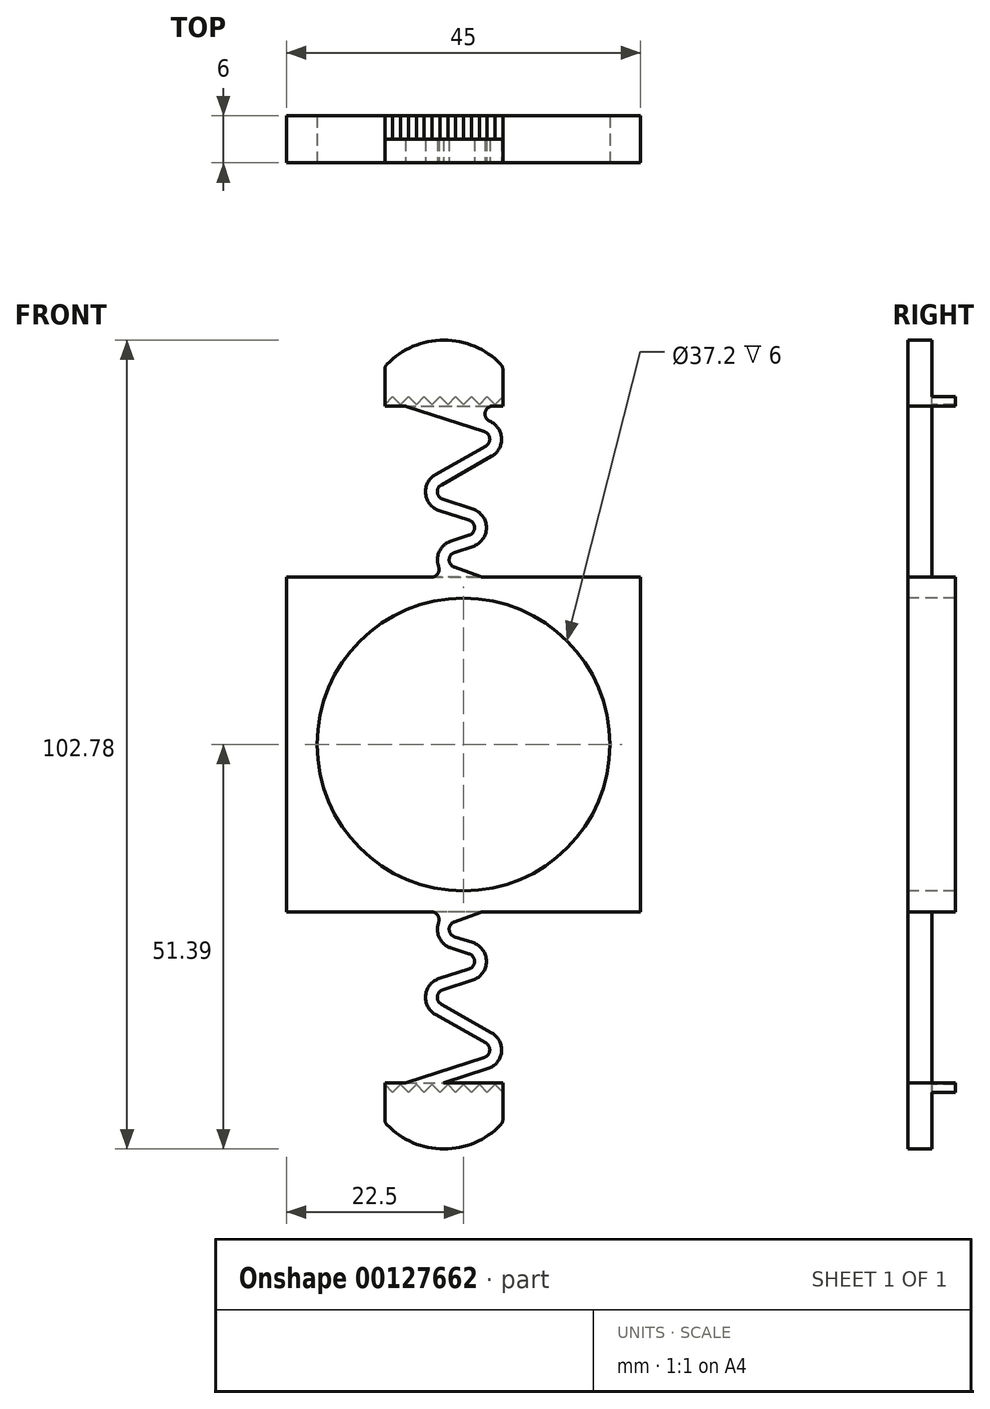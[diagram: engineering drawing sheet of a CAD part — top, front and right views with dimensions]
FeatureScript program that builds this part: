
annotation { "Feature Type Name" : "Feature", "Feature Type Description" : "" }
export const myFeature = defineFeature(function(context is Context, id is Id, definition is map)
    precondition{}
    {
        {
            var Q0;
            Q0=qCreatedBy(makeId("Right.planeOp"),FACE);
            var sketch = newSketch(context, id + "F0", { "sketchPlane" : qUnion([Q0])});
            skLineSegment(sketch, "E0", {"start": v(0, 25) * mm, "end": v(0, -25) * mm});
            skLineSegment(sketch, "E1", {"start": v(0, -25) * mm, "end": v(-3, -25) * mm});
            skLineSegment(sketch, "E2", {"start": v(-3, -25) * mm, "end": v(-3, -21.25) * mm});
            skLineSegment(sketch, "E3", {"start": v(-3, -21.25) * mm, "end": v(-9, -21.25) * mm});
            skLineSegment(sketch, "E4", {"start": v(-9, -21.25) * mm, "end": v(-9, 21.25) * mm});
            skLineSegment(sketch, "E5", {"start": v(-9, 21.25) * mm, "end": v(-3, 21.25) * mm});
            skLineSegment(sketch, "E6", {"start": v(-3, 21.25) * mm, "end": v(-3, 25) * mm});
            skLineSegment(sketch, "E7", {"start": v(-3, 25) * mm, "end": v(0, 25) * mm});
            skSolve(sketch);
        }
        {
            var Q0;
            Q0 = qSketchRegion(id + "F0", true);
            extrude(context, id + "F1", {"entities" : qUnion([Q0]), "endBound" : BoundingType.SYMMETRIC, "depth" : 45 * mm});
        }
        {
            var Q0;
            Q0=makeQuery(id+"F1.opExtrude","SWEPT_FACE",FACE,{"disambiguationData":[OSD([sQuery(id+"F0.wireOp",EDGE,"E4")])]});
            var sketch = newSketch(context, id + "F2", { "sketchPlane" : qUnion([Q0])});
            skCircle(sketch, "E8", {"center": v(0, 0) * mm, "radius": 18.6 * mm});
            skSolve(sketch);
        }
        {
            var Q0;
            Q0 = qSketchRegion(id + "F2", true);
            extrude(context, id + "F3", {"entities" : qUnion([Q0]), "operationType" : NewBodyOperationType.REMOVE, "oppositeDirection" : true, "depth" : 6 * mm});
        }
        {
            var Q0;
            Q0=makeQuery(id+"F3.boolean.opBoolean","COPY",FACE,{"derivedFrom":makeQuery(id+"F3.opExtrude","CAP_FACE",FACE,{"disambiguationData":[OSD([sQuery(id+"F2.wireOp",EDGE,"E8")])],"isStart":false})});
            var sketch = newSketch(context, id + "F4", { "sketchPlane" : qUnion([Q0])});
            skCircle(sketch, "E9", {"center": v(0, 0) * mm, "radius": 17.5 * mm});
            skSolve(sketch);
        }
        {
            var Q0;
            Q0 = qSketchRegion(id + "F4", true);
            extrude(context, id + "F5", {"entities" : qUnion([Q0]), "operationType" : NewBodyOperationType.REMOVE, "endBound" : BoundingType.UP_TO_NEXT, "oppositeDirection" : true, "depth" : 25 * mm});
        }
        {
            var Q0;
            Q0=makeQuery(id+"F1.opExtrude","SWEPT_FACE",FACE,{"disambiguationData":[OSD([sQuery(id+"F0.wireOp",EDGE,"E4")])]});
            var sketch = newSketch(context, id + "F6", { "sketchPlane" : qUnion([Q0])});
            skLineSegment(sketch, "E10", {"start": v(0, 43.5) * mm, "end": v(0, -43.5) * mm, "construction": true});
            skLineSegment(sketch, "E11", {"start": v(-1.5, 21.05) * mm, "end": v(-1.68, 21.11) * mm});
            skLineSegment(sketch, "E12", {"start": v(-1.6, 25.84) * mm, "end": v(0.72, 26.6) * mm});
            skLineSegment(sketch, "E13", {"start": v(0.72, 28.5) * mm, "end": v(-3.1, 29.74) * mm});
            skLineSegment(sketch, "E14", {"start": v(-3.57, 34.29) * mm, "end": v(2.83, 37.92) * mm});
            skLineSegment(sketch, "E15", {"start": v(2.64, 39.74) * mm, "end": v(-8.93, 43.5) * mm});
            skLineSegment(sketch, "E16", {"start": v(-8.5, 31.5) * mm, "end": v(-8.5, 23.6) * mm, "construction": true});
            skLineSegment(sketch, "E17", {"start": v(-1.13, 24.41) * mm, "end": v(1.18, 25.17) * mm});
            skLineSegment(sketch, "E18", {"start": v(1.18, 29.92) * mm, "end": v(-2.64, 31.16) * mm});
            skLineSegment(sketch, "E19", {"start": v(-2.83, 32.99) * mm, "end": v(3.57, 36.61) * mm});
            skLineSegment(sketch, "E20", {"start": v(3.1, 41.17) * mm, "end": v(-4.08, 43.5) * mm});
            skLineSegment(sketch, "E21", {"start": v(8.5, 39.41) * mm, "end": v(8.5, 27.54) * mm, "construction": true});
            skLineSegment(sketch, "E22", {"start": v(-8.93, 43.5) * mm, "end": v(-4.08, 43.5) * mm});
            skPoint(sketch, "E23.visualSharp", {"position": v(-4.8, 31.87) * mm});
            skArc(sketch, "E23.filletArc", {"start": v(-2.83, 32.99) * mm, "mid": v(-3.33, 32.01) * mm, "end": v(-2.64, 31.16) * mm});
            skPoint(sketch, "E24.visualSharp", {"position": v(-4.56, 23.3) * mm});
            skArc(sketch, "E24.filletArc", {"start": v(-1.13, 24.41) * mm, "mid": v(-1.82, 23.48) * mm, "end": v(-1.16, 22.52) * mm});
            skPoint(sketch, "E25.visualSharp", {"position": v(3.65, 27.54) * mm});
            skArc(sketch, "E25.filletArc", {"start": v(0.72, 26.6) * mm, "mid": v(1.4, 27.54) * mm, "end": v(0.72, 28.5) * mm});
            skPoint(sketch, "E26.visualSharp", {"position": v(4.8, 39.04) * mm});
            skArc(sketch, "E26.filletArc", {"start": v(2.83, 37.92) * mm, "mid": v(3.33, 38.89) * mm, "end": v(2.64, 39.74) * mm});
            skPoint(sketch, "E27.visualSharp", {"position": v(8.5, 39.41) * mm});
            skArc(sketch, "E27.filletArc", {"start": v(3.57, 36.61) * mm, "mid": v(4.82, 39.04) * mm, "end": v(3.1, 41.17) * mm});
            skPoint(sketch, "E28.visualSharp", {"position": v(-8.5, 31.5) * mm});
            skArc(sketch, "E28.filletArc", {"start": v(-3.57, 34.29) * mm, "mid": v(-4.82, 31.86) * mm, "end": v(-3.1, 29.74) * mm});
            skPoint(sketch, "E29.visualSharp", {"position": v(8.5, 27.54) * mm});
            skArc(sketch, "E29.filletArc", {"start": v(1.18, 25.17) * mm, "mid": v(2.9, 27.54) * mm, "end": v(1.18, 29.92) * mm});
            skPoint(sketch, "E30.visualSharp", {"position": v(-8.5, 23.6) * mm});
            skArc(sketch, "E30.filletArc", {"start": v(-1.6, 25.84) * mm, "mid": v(-3.32, 23.5) * mm, "end": v(-1.68, 21.11) * mm});
            skLineSegment(sketch, "E31", {"start": v(0, 0) * mm, "end": v(22.5, 0) * mm, "construction": true});
            skArc(sketch, "E32.MirrorCS", {"start": v(-2.83, -32.99) * mm, "mid": v(-3.33, -32.01) * mm, "end": v(-2.64, -31.16) * mm});
            skArc(sketch, "E33.MirrorCS", {"start": v(2.83, -37.92) * mm, "mid": v(3.33, -38.89) * mm, "end": v(2.64, -39.74) * mm});
            skArc(sketch, "E34.MirrorCS", {"start": v(-1.13, -24.41) * mm, "mid": v(-1.82, -23.48) * mm, "end": v(-1.16, -22.52) * mm});
            skLineSegment(sketch, "E35.MirrorCS", {"start": v(3.1, -41.17) * mm, "end": v(-4.08, -43.5) * mm});
            skLineSegment(sketch, "E36.MirrorCS", {"start": v(-1.5, -21.05) * mm, "end": v(-1.68, -21.11) * mm});
            skArc(sketch, "E37.MirrorCS", {"start": v(0.72, -26.6) * mm, "mid": v(1.4, -27.54) * mm, "end": v(0.72, -28.5) * mm});
            skArc(sketch, "E38.MirrorCS", {"start": v(1.18, -25.17) * mm, "mid": v(2.9, -27.54) * mm, "end": v(1.18, -29.92) * mm});
            skArc(sketch, "E39.MirrorCS", {"start": v(3.57, -36.61) * mm, "mid": v(4.82, -39.04) * mm, "end": v(3.1, -41.17) * mm});
            skArc(sketch, "E40.MirrorCS", {"start": v(-3.57, -34.29) * mm, "mid": v(-4.82, -31.86) * mm, "end": v(-3.1, -29.74) * mm});
            skLineSegment(sketch, "E41.MirrorCS", {"start": v(-1.13, -24.41) * mm, "end": v(1.18, -25.17) * mm});
            skLineSegment(sketch, "E42.MirrorCS", {"start": v(-2.83, -32.99) * mm, "end": v(3.57, -36.61) * mm});
            skLineSegment(sketch, "E43.MirrorCS", {"start": v(2.64, -39.74) * mm, "end": v(-8.93, -43.5) * mm});
            skLineSegment(sketch, "E44.MirrorCS", {"start": v(-3.57, -34.29) * mm, "end": v(2.83, -37.92) * mm});
            skLineSegment(sketch, "E45.MirrorCS", {"start": v(0.72, -28.5) * mm, "end": v(-3.1, -29.74) * mm});
            skLineSegment(sketch, "E46.MirrorCS", {"start": v(-1.6, -25.84) * mm, "end": v(0.72, -26.6) * mm});
            skPoint(sketch, "E47.MirrorP", {"position": v(-4.56, -23.3) * mm});
            skPoint(sketch, "E48.MirrorP", {"position": v(4.8, -39.04) * mm});
            skLineSegment(sketch, "E49.MirrorCS", {"start": v(-8.93, -43.5) * mm, "end": v(-4.08, -43.5) * mm});
            skLineSegment(sketch, "E50.MirrorCS", {"start": v(1.18, -29.92) * mm, "end": v(-2.64, -31.16) * mm});
            skPoint(sketch, "E51.MirrorP", {"position": v(-8.5, -31.5) * mm});
            skPoint(sketch, "E52.MirrorP", {"position": v(8.5, -27.54) * mm});
            skPoint(sketch, "E53.MirrorP", {"position": v(3.65, -27.54) * mm});
            skPoint(sketch, "E54.MirrorP", {"position": v(8.5, -39.41) * mm});
            skPoint(sketch, "E55.MirrorP", {"position": v(-8.5, -23.6) * mm});
            skArc(sketch, "E56.MirrorCS", {"start": v(-1.6, -25.84) * mm, "mid": v(-3.32, -23.5) * mm, "end": v(-1.68, -21.11) * mm});
            skPoint(sketch, "E57.MirrorP", {"position": v(-4.8, -31.87) * mm});
            skPoint(sketch, "E58.orphan", {"position": v(1.5, 21.25) * mm});
            skLineSegment(sketch, "E59", {"start": v(-1.5, 21.05) * mm, "end": v(2.89, 21.05) * mm});
            skLineSegment(sketch, "E60", {"start": v(2.89, 21.05) * mm, "end": v(-1.16, 22.52) * mm});
            skLineSegment(sketch, "E61", {"start": v(-1.5, -21.05) * mm, "end": v(2.89, -21.05) * mm});
            skLineSegment(sketch, "E62", {"start": v(2.89, -21.05) * mm, "end": v(-1.16, -22.52) * mm});
            skSolve(sketch);
        }
        {
            var Q0;
            Q0 = qSketchRegion(id + "F6", true);
            extrude(context, id + "F7", {"entities" : qUnion([Q0]), "operationType" : NewBodyOperationType.ADD, "oppositeDirection" : true, "depth" : 3 * mm});
        }
        {
            var Q0;
            Q0=makeQuery(id+"F7.boolean.opBoolean","MERGE",FACE,{"derivedFrom":[makeQuery(id+"F1.opExtrude","SWEPT_FACE",FACE,{"disambiguationData":[OSD([sQuery(id+"F0.wireOp",EDGE,"E4")])]}),makeQuery(id+"F7.opExtrude","CAP_FACE",FACE,{"disambiguationData":[OSD([sQuery(id+"F6.wireOp",EDGE,"E11"),sQuery(id+"F6.wireOp",EDGE,"E12"),sQuery(id+"F6.wireOp",EDGE,"E13"),sQuery(id+"F6.wireOp",EDGE,"E14"),sQuery(id+"F6.wireOp",EDGE,"E15"),sQuery(id+"F6.wireOp",EDGE,"E17"),sQuery(id+"F6.wireOp",EDGE,"E18"),sQuery(id+"F6.wireOp",EDGE,"E19"),sQuery(id+"F6.wireOp",EDGE,"E20"),sQuery(id+"F6.wireOp",EDGE,"E22"),sQuery(id+"F6.wireOp",EDGE,"E23.filletArc"),sQuery(id+"F6.wireOp",EDGE,"E24.filletArc"),sQuery(id+"F6.wireOp",EDGE,"E25.filletArc"),sQuery(id+"F6.wireOp",EDGE,"E26.filletArc"),sQuery(id+"F6.wireOp",EDGE,"E27.filletArc"),sQuery(id+"F6.wireOp",EDGE,"E28.filletArc"),sQuery(id+"F6.wireOp",EDGE,"E29.filletArc"),sQuery(id+"F6.wireOp",EDGE,"E30.filletArc"),sQuery(id+"F6.wireOp",EDGE,"E59"),sQuery(id+"F6.wireOp",EDGE,"E60")])],"isStart":true}),makeQuery(id+"F7.opExtrude","CAP_FACE",FACE,{"disambiguationData":[OSD([sQuery(id+"F6.wireOp",EDGE,"E32.MirrorCS"),sQuery(id+"F6.wireOp",EDGE,"E33.MirrorCS"),sQuery(id+"F6.wireOp",EDGE,"E34.MirrorCS"),sQuery(id+"F6.wireOp",EDGE,"E35.MirrorCS"),sQuery(id+"F6.wireOp",EDGE,"E36.MirrorCS"),sQuery(id+"F6.wireOp",EDGE,"E37.MirrorCS"),sQuery(id+"F6.wireOp",EDGE,"E38.MirrorCS"),sQuery(id+"F6.wireOp",EDGE,"E39.MirrorCS"),sQuery(id+"F6.wireOp",EDGE,"E40.MirrorCS"),sQuery(id+"F6.wireOp",EDGE,"E41.MirrorCS"),sQuery(id+"F6.wireOp",EDGE,"E42.MirrorCS"),sQuery(id+"F6.wireOp",EDGE,"E43.MirrorCS"),sQuery(id+"F6.wireOp",EDGE,"E44.MirrorCS"),sQuery(id+"F6.wireOp",EDGE,"E45.MirrorCS"),sQuery(id+"F6.wireOp",EDGE,"E46.MirrorCS"),sQuery(id+"F6.wireOp",EDGE,"E49.MirrorCS"),sQuery(id+"F6.wireOp",EDGE,"E50.MirrorCS"),sQuery(id+"F6.wireOp",EDGE,"E56.MirrorCS"),sQuery(id+"F6.wireOp",EDGE,"E61"),sQuery(id+"F6.wireOp",EDGE,"E62")])],"isStart":true})]});
            var sketch = newSketch(context, id + "F11", { "sketchPlane" : qUnion([Q0])});
            skLineSegment(sketch, "E63", {"start": v(-10, 43) * mm, "end": v(5, 43) * mm});
            skLineSegment(sketch, "E64", {"start": v(-10, 43) * mm, "end": v(-10, 47.61) * mm});
            skLineSegment(sketch, "E65", {"start": v(5, 47.61) * mm, "end": v(5, 43) * mm});
            skArc(sketch, "E66", {"start": v(4.72, 48.3) * mm, "mid": v(-2.5, 51.39) * mm, "end": v(-9.72, 48.3) * mm});
            skLineSegment(sketch, "E67", {"start": v(-2.5, 43.5) * mm, "end": v(-2.5, 43) * mm, "construction": true});
            skPoint(sketch, "E68.visualSharp", {"position": v(-11.33, 62.8) * mm});
            skPoint(sketch, "E69.visualSharp", {"position": v(-10, 48) * mm});
            skArc(sketch, "E69.filletArc", {"start": v(-9.72, 48.3) * mm, "mid": v(-9.93, 47.98) * mm, "end": v(-10, 47.61) * mm});
            skPoint(sketch, "E70.visualSharp", {"position": v(5, 48) * mm});
            skArc(sketch, "E70.filletArc", {"start": v(5, 47.61) * mm, "mid": v(4.93, 47.98) * mm, "end": v(4.72, 48.3) * mm});
            skLineSegment(sketch, "E71", {"start": v(0, 0) * mm, "end": v(18.6, 0) * mm, "construction": true});
            skLineSegment(sketch, "E72", {"start": v(-2.5, 47.61) * mm, "end": v(-2.5, 51.39) * mm, "construction": true});
            skLineSegment(sketch, "E73", {"start": v(-2.5, 47.61) * mm, "end": v(-10, 47.61) * mm, "construction": true});
            skPoint(sketch, "E74.MirrorCS.end.orphan", {"position": v(5, -43) * mm});
            skPoint(sketch, "E74.MirrorCS.start.orphan", {"position": v(-10, -43) * mm});
            skPoint(sketch, "E75.MirrorCS.end.orphan", {"position": v(-10, -47.61) * mm});
            skPoint(sketch, "E76.MirrorCS.start.orphan", {"position": v(5, -47.61) * mm});
            skPoint(sketch, "E77.MirrorCS.end.orphan", {"position": v(-9.72, -48.3) * mm});
            skPoint(sketch, "E77.MirrorCS.start.orphan", {"position": v(4.72, -48.3) * mm});
            skLineSegment(sketch, "E78.MirrorCS", {"start": v(-10, -43) * mm, "end": v(5, -43) * mm});
            skLineSegment(sketch, "E79.MirrorCS", {"start": v(-10, -43) * mm, "end": v(-10, -47.61) * mm});
            skArc(sketch, "E80.MirrorCS", {"start": v(4.72, -48.3) * mm, "mid": v(-2.5, -51.39) * mm, "end": v(-9.72, -48.3) * mm});
            skLineSegment(sketch, "E81.MirrorCS", {"start": v(5, -47.61) * mm, "end": v(5, -43) * mm});
            skArc(sketch, "E82.MirrorCS", {"start": v(5, -47.61) * mm, "mid": v(4.93, -47.98) * mm, "end": v(4.72, -48.3) * mm});
            skArc(sketch, "E83.MirrorCS", {"start": v(-9.72, -48.3) * mm, "mid": v(-9.93, -47.98) * mm, "end": v(-10, -47.61) * mm});
            skSolve(sketch);
        }
        {
            var Q0;
            Q0 = qSketchRegion(id + "F11", true);
            extrude(context, id + "F8", {"entities" : qUnion([Q0]), "operationType" : NewBodyOperationType.ADD, "oppositeDirection" : true, "depth" : 3 * mm});
        }
        {
            var Q0;
            Q0=makeQuery(id+"F8.boolean.opBoolean","MERGE",FACE,{"derivedFrom":[makeQuery(id+"F7.opExtrude","CAP_FACE",FACE,{"disambiguationData":[OSD([sQuery(id+"F6.wireOp",EDGE,"E11"),sQuery(id+"F6.wireOp",EDGE,"E12"),sQuery(id+"F6.wireOp",EDGE,"E13"),sQuery(id+"F6.wireOp",EDGE,"E14"),sQuery(id+"F6.wireOp",EDGE,"E15"),sQuery(id+"F6.wireOp",EDGE,"E17"),sQuery(id+"F6.wireOp",EDGE,"E18"),sQuery(id+"F6.wireOp",EDGE,"E19"),sQuery(id+"F6.wireOp",EDGE,"E20"),sQuery(id+"F6.wireOp",EDGE,"E22"),sQuery(id+"F6.wireOp",EDGE,"E23.filletArc"),sQuery(id+"F6.wireOp",EDGE,"E24.filletArc"),sQuery(id+"F6.wireOp",EDGE,"E25.filletArc"),sQuery(id+"F6.wireOp",EDGE,"E26.filletArc"),sQuery(id+"F6.wireOp",EDGE,"E27.filletArc"),sQuery(id+"F6.wireOp",EDGE,"E28.filletArc"),sQuery(id+"F6.wireOp",EDGE,"E29.filletArc"),sQuery(id+"F6.wireOp",EDGE,"E30.filletArc"),sQuery(id+"F6.wireOp",EDGE,"E59"),sQuery(id+"F6.wireOp",EDGE,"E60")])],"isStart":false}),makeQuery(id+"F8.opExtrude","CAP_FACE",FACE,{"disambiguationData":[OSD([sQuery(id+"F11.wireOp",EDGE,"E63"),sQuery(id+"F11.wireOp",EDGE,"E64"),sQuery(id+"F11.wireOp",EDGE,"E65"),sQuery(id+"F11.wireOp",EDGE,"E66"),sQuery(id+"F11.wireOp",EDGE,"E69.filletArc"),sQuery(id+"F11.wireOp",EDGE,"E70.filletArc")])],"isStart":false})]});
            var sketch = newSketch(context, id + "F12", { "sketchPlane" : qUnion([Q0])});
            skLineSegment(sketch, "E84", {"start": v(10, 43) * mm, "end": v(10, 43.2) * mm});
            skLineSegment(sketch, "E85", {"start": v(10, 43.2) * mm, "end": v(9, 44.2) * mm});
            skLineSegment(sketch, "E86", {"start": v(9, 44.2) * mm, "end": v(8, 43.2) * mm});
            skLineSegment(sketch, "E87", {"start": v(8, 43.2) * mm, "end": v(7, 44.2) * mm});
            skLineSegment(sketch, "E88", {"start": v(7, 44.2) * mm, "end": v(6, 43.2) * mm});
            skLineSegment(sketch, "E89", {"start": v(6, 43.2) * mm, "end": v(5, 44.2) * mm});
            skLineSegment(sketch, "E90", {"start": v(4, 43.2) * mm, "end": v(5, 44.2) * mm});
            skLineSegment(sketch, "E91", {"start": v(4, 43.2) * mm, "end": v(3, 44.2) * mm});
            skLineSegment(sketch, "E92", {"start": v(3, 44.2) * mm, "end": v(2, 43.2) * mm});
            skLineSegment(sketch, "E93", {"start": v(2, 43.2) * mm, "end": v(1, 44.2) * mm});
            skLineSegment(sketch, "E94", {"start": v(1, 44.2) * mm, "end": v(0, 43.2) * mm});
            skLineSegment(sketch, "E95", {"start": v(0, 43.2) * mm, "end": v(-1, 44.2) * mm});
            skLineSegment(sketch, "E96", {"start": v(-1, 44.2) * mm, "end": v(-2, 43.2) * mm});
            skLineSegment(sketch, "E97", {"start": v(-2, 43.2) * mm, "end": v(-3, 44.2) * mm});
            skLineSegment(sketch, "E98", {"start": v(-3, 44.2) * mm, "end": v(-4, 43.2) * mm});
            skLineSegment(sketch, "E99", {"start": v(-4, 43.2) * mm, "end": v(-5, 44.2) * mm});
            skLineSegment(sketch, "E100", {"start": v(-5, 44.2) * mm, "end": v(-5, 43) * mm});
            skPoint(sketch, "E101.end.orphan", {"position": v(-6, 43.2) * mm});
            skLineSegment(sketch, "E102", {"start": v(10, 43) * mm, "end": v(-5, 43) * mm});
            skLineSegment(sketch, "E103", {"start": v(0, 0) * mm, "end": v(17.5, 0) * mm, "construction": true});
            skLineSegment(sketch, "E104.MirrorCS", {"start": v(-5, -44.2) * mm, "end": v(-5, -43) * mm});
            skLineSegment(sketch, "E105.MirrorCS", {"start": v(-4, -43.2) * mm, "end": v(-5, -44.2) * mm});
            skLineSegment(sketch, "E106.MirrorCS", {"start": v(10, -43) * mm, "end": v(-5, -43) * mm});
            skLineSegment(sketch, "E107.MirrorCS", {"start": v(-3, -44.2) * mm, "end": v(-4, -43.2) * mm});
            skLineSegment(sketch, "E108.MirrorCS", {"start": v(-2, -43.2) * mm, "end": v(-3, -44.2) * mm});
            skLineSegment(sketch, "E109.MirrorCS", {"start": v(-1, -44.2) * mm, "end": v(-2, -43.2) * mm});
            skLineSegment(sketch, "E110.MirrorCS", {"start": v(0, -43.2) * mm, "end": v(-1, -44.2) * mm});
            skLineSegment(sketch, "E111.MirrorCS", {"start": v(1, -44.2) * mm, "end": v(0, -43.2) * mm});
            skLineSegment(sketch, "E112.MirrorCS", {"start": v(2, -43.2) * mm, "end": v(1, -44.2) * mm});
            skLineSegment(sketch, "E113.MirrorCS", {"start": v(3, -44.2) * mm, "end": v(2, -43.2) * mm});
            skLineSegment(sketch, "E114.MirrorCS", {"start": v(4, -43.2) * mm, "end": v(3, -44.2) * mm});
            skLineSegment(sketch, "E115.MirrorCS", {"start": v(4, -43.2) * mm, "end": v(5, -44.2) * mm});
            skLineSegment(sketch, "E116.MirrorCS", {"start": v(6, -43.2) * mm, "end": v(5, -44.2) * mm});
            skLineSegment(sketch, "E117.MirrorCS", {"start": v(8, -43.2) * mm, "end": v(7, -44.2) * mm});
            skLineSegment(sketch, "E118.MirrorCS", {"start": v(7, -44.2) * mm, "end": v(6, -43.2) * mm});
            skLineSegment(sketch, "E119.MirrorCS", {"start": v(9, -44.2) * mm, "end": v(8, -43.2) * mm});
            skLineSegment(sketch, "E120.MirrorCS", {"start": v(10, -43.2) * mm, "end": v(9, -44.2) * mm});
            skLineSegment(sketch, "E121.MirrorCS", {"start": v(10, -43) * mm, "end": v(10, -43.2) * mm});
            skSolve(sketch);
        }
        {
            var Q0;
            Q0 = qSketchRegion(id + "F12", true);
            extrude(context, id + "F13", {"entities" : qUnion([Q0]), "operationType" : NewBodyOperationType.ADD, "depth" : 3 * mm});
        }
        {
            var Q0;
            Q0=makeQuery(id+"F7.boolean.opBoolean","INTERSECT",EDGE,{"derivedFrom":[makeQuery(id+"F1.opExtrude","SWEPT_FACE",FACE,{"disambiguationData":[OSD([sQuery(id+"F0.wireOp",EDGE,"E5")])]}),makeQuery(id+"F7.opExtrude","SWEPT_FACE",FACE,{"disambiguationData":[OSD([sQuery(id+"F6.wireOp",EDGE,"E30.filletArc")])]})]});
            var Q1;
            Q1=makeQuery(id+"F7.boolean.opBoolean","INTERSECT",EDGE,{"derivedFrom":[makeQuery(id+"F1.opExtrude","SWEPT_FACE",FACE,{"disambiguationData":[OSD([sQuery(id+"F0.wireOp",EDGE,"E5")])]}),makeQuery(id+"F7.opExtrude","SWEPT_FACE",FACE,{"disambiguationData":[OSD([sQuery(id+"F6.wireOp",EDGE,"E60")])]})]});
            var Q2;
            Q2=makeQuery(id+"F8.boolean.opBoolean","INTERSECT",EDGE,{"derivedFrom":[makeQuery(id+"F7.opExtrude","SWEPT_FACE",FACE,{"disambiguationData":[OSD([sQuery(id+"F6.wireOp",EDGE,"E15")])]}),makeQuery(id+"F8.opExtrude","SWEPT_FACE",FACE,{"disambiguationData":[OSD([sQuery(id+"F11.wireOp",EDGE,"E63")])]})]});
            var Q3;
            Q3=makeQuery(id+"F8.boolean.opBoolean","INTERSECT",EDGE,{"derivedFrom":[makeQuery(id+"F7.opExtrude","SWEPT_FACE",FACE,{"disambiguationData":[OSD([sQuery(id+"F6.wireOp",EDGE,"E20")])]}),makeQuery(id+"F8.opExtrude","SWEPT_FACE",FACE,{"disambiguationData":[OSD([sQuery(id+"F11.wireOp",EDGE,"E63")])]})]});
            var Q4;
            Q4=makeQuery(id+"F7.boolean.opBoolean","INTERSECT",EDGE,{"derivedFrom":[makeQuery(id+"F1.opExtrude","SWEPT_FACE",FACE,{"disambiguationData":[OSD([sQuery(id+"F0.wireOp",EDGE,"E3")])]}),makeQuery(id+"F7.opExtrude","SWEPT_FACE",FACE,{"disambiguationData":[OSD([sQuery(id+"F6.wireOp",EDGE,"E56.MirrorCS")])]})]});
            var Q5;
            Q5=makeQuery(id+"F8.boolean.opBoolean","INTERSECT",EDGE,{"derivedFrom":[makeQuery(id+"F7.opExtrude","SWEPT_FACE",FACE,{"disambiguationData":[OSD([sQuery(id+"F6.wireOp",EDGE,"E43.MirrorCS")])]}),makeQuery(id+"F8.opExtrude","SWEPT_FACE",FACE,{"disambiguationData":[OSD([sQuery(id+"F11.wireOp",EDGE,"E74.MirrorCS")])]})]});
            var Q6;
            Q6=makeQuery(id+"F7.boolean.opBoolean","INTERSECT",EDGE,{"derivedFrom":[makeQuery(id+"F1.opExtrude","SWEPT_FACE",FACE,{"disambiguationData":[OSD([sQuery(id+"F0.wireOp",EDGE,"E3")])]}),makeQuery(id+"F7.opExtrude","SWEPT_FACE",FACE,{"disambiguationData":[OSD([sQuery(id+"F6.wireOp",EDGE,"E62")])]})]});
            var Q7;
            Q7=makeQuery(id+"F8.boolean.opBoolean","INTERSECT",EDGE,{"derivedFrom":[makeQuery(id+"F7.opExtrude","SWEPT_FACE",FACE,{"disambiguationData":[OSD([sQuery(id+"F6.wireOp",EDGE,"E35.MirrorCS")])]}),makeQuery(id+"F8.opExtrude","SWEPT_FACE",FACE,{"disambiguationData":[OSD([sQuery(id+"F11.wireOp",EDGE,"E74.MirrorCS")])]})]});
            fillet(context, id + "F9", {"entities" : qUnion([Q0, Q1, Q2, Q3, Q4, Q5, Q6, Q7]), "radius" : 1 * mm, "tangentPropagation" : true, "allowEdgeOverflow" : false});
        }
        {
            var Q0;
            Q0=makeQuery(id+"F1.opExtrude","CAP_FACE",FACE,{"disambiguationData":[OSD([sQuery(id+"F0.wireOp",EDGE,"E0"),sQuery(id+"F0.wireOp",EDGE,"E1"),sQuery(id+"F0.wireOp",EDGE,"E2"),sQuery(id+"F0.wireOp",EDGE,"E3"),sQuery(id+"F0.wireOp",EDGE,"E4"),sQuery(id+"F0.wireOp",EDGE,"E5"),sQuery(id+"F0.wireOp",EDGE,"E6"),sQuery(id+"F0.wireOp",EDGE,"E7")])],"isStart":false});
            var sketch = newSketch(context, id + "F14", { "sketchPlane" : qUnion([Q0])});
            skLineSegment(sketch, "E122.bottom", {"start": v(0, -25) * mm, "end": v(-3, -25) * mm});
            skLineSegment(sketch, "E122.top", {"start": v(0, 25) * mm, "end": v(-3, 25) * mm});
            skLineSegment(sketch, "E122.left", {"start": v(0, -25) * mm, "end": v(0, 25) * mm});
            skLineSegment(sketch, "E122.right", {"start": v(-3, -25) * mm, "end": v(-3, 25) * mm});
            skSolve(sketch);
        }
        {
            var Q0;
            Q0 = qSketchRegion(id + "F14", true);
            extrude(context, id + "F10", {"entities" : qUnion([Q0]), "operationType" : NewBodyOperationType.REMOVE, "endBound" : BoundingType.THROUGH_ALL, "oppositeDirection" : true, "depth" : 25 * mm});
        }
    });
